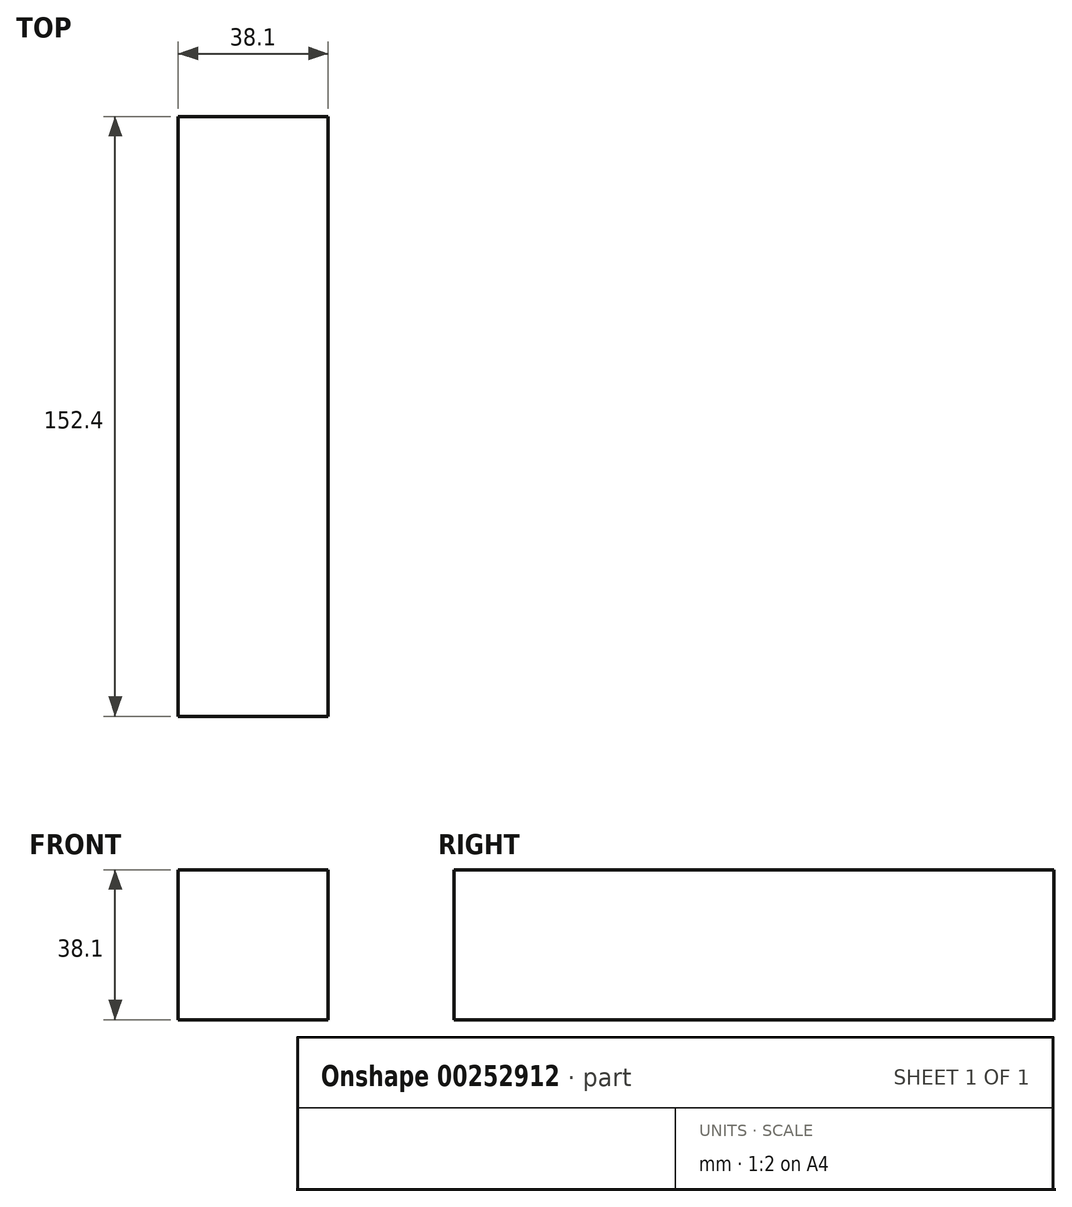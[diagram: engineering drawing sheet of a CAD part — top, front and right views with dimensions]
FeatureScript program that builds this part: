
annotation { "Feature Type Name" : "Feature", "Feature Type Description" : "" }
export const myFeature = defineFeature(function(context is Context, id is Id, definition is map)
    precondition{}
    {
        {
            var Q0;
            Q0=qCreatedBy(makeId("Front.planeOp"),FACE);
            var sketch = newSketch(context, id + "F0", { "sketchPlane" : qUnion([Q0])});
            skLineSegment(sketch, "E0", {"start": v(0, 0) * mm, "end": v(38.1, 0) * mm});
            skLineSegment(sketch, "E1", {"start": v(38.1, 0) * mm, "end": v(38.1, 38.1) * mm});
            skLineSegment(sketch, "E2", {"start": v(38.1, 38.1) * mm, "end": v(0, 38.1) * mm});
            skLineSegment(sketch, "E3", {"start": v(0, 38.1) * mm, "end": v(0, 0) * mm});
            skSolve(sketch);
        }
        {
            var Q0;
            Q0=makeQuery(id+"F0.imprint","IMPRINT",FACE,{"disambiguationData":[TD([[makeQuery(id+"F0.imprint","IMPRINT",EDGE,{"derivedFrom":sQuery(id+"F0.wireOp",EDGE,"E0")}),1.0]])]});
            extrude(context, id + "F1", {"entities" : qUnion([Q0]), "depth" : 152.4 * mm});
        }
    });
